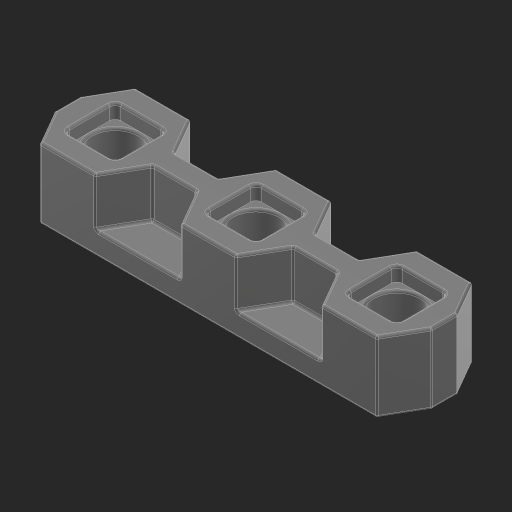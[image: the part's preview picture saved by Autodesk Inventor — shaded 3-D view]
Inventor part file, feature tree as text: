
AUTODESK INVENTOR PART (.ipt)
format: ipt  version: 2023 (Build 270158000, 158)  size: 339,968 bytes
history: native  units: in
note: dims shown in document units (in); Inventor stores cm internally (conversion verified against a paired STEP export)
features: fillet x1
ambient origin geometry x8: Origin, YZ Plane, XZ Plane, XY Plane, X Axis, Y Axis, Z Axis, Center Point
bodies: Solid1 (feature_tree)
feature tree (1):
  fillet  "Fillet6"  [1 undecoded]
note: 1 required parameter value undecoded (feature->parameter linkage not recoverable at this tier; creation-order binding heuristic only, values carry confidence <= 0.55)
